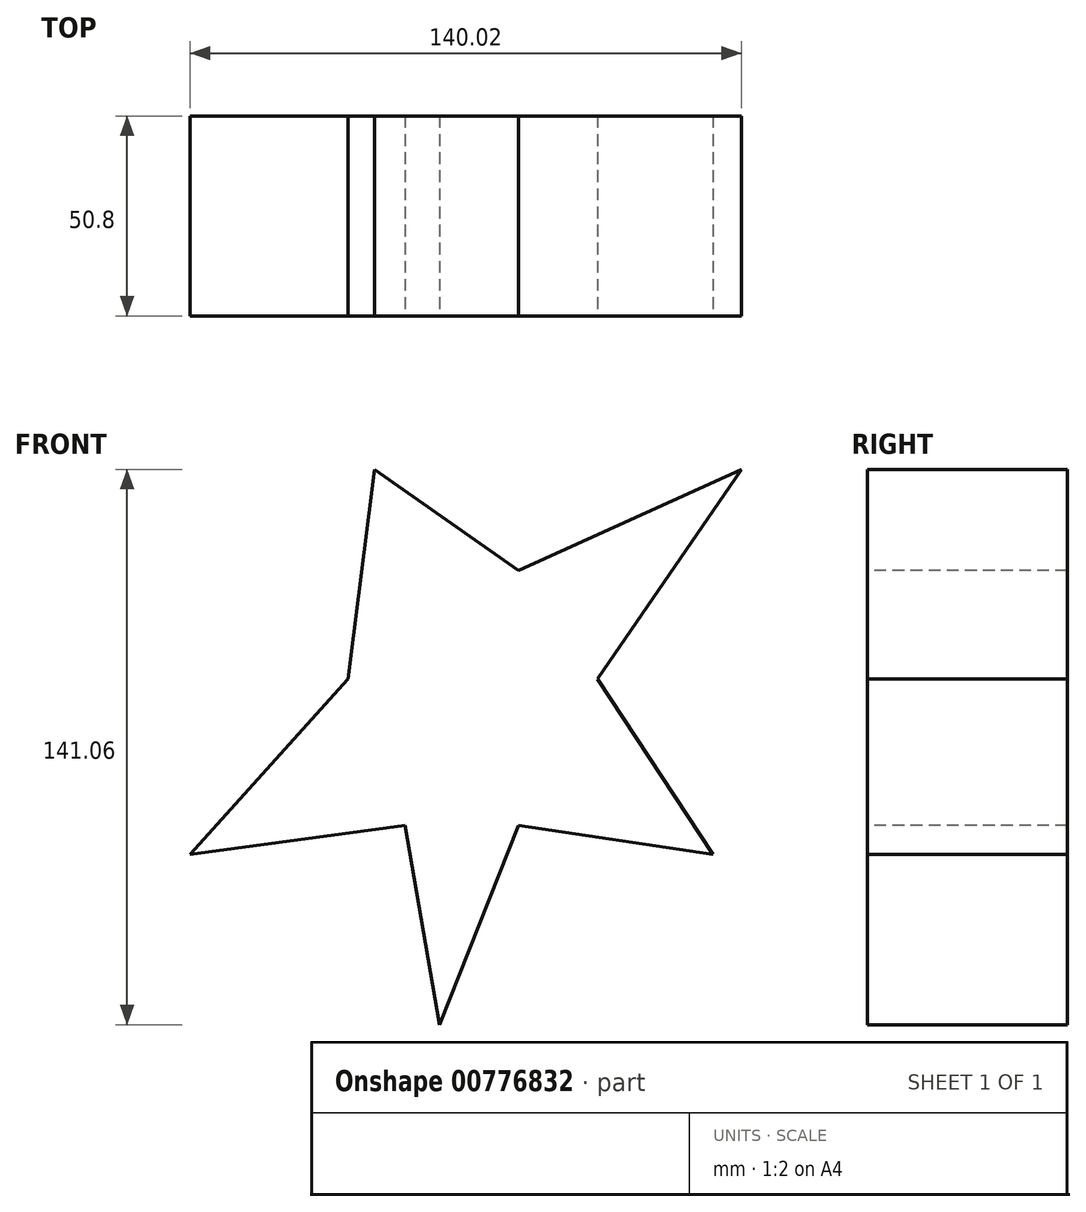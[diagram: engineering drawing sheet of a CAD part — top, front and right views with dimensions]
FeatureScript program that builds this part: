
annotation { "Feature Type Name" : "Feature", "Feature Type Description" : "" }
export const myFeature = defineFeature(function(context is Context, id is Id, definition is map)
    precondition{}
    {
        {
            var Q0;
            Q0=qCreatedBy(makeId("Front.planeOp"),FACE);
            var sketch = newSketch(context, id + "F0", { "sketchPlane" : qUnion([Q0])});
            skLineSegment(sketch, "E0", {"start": v(-6.95, -50.65) * mm, "end": v(13.13, 0) * mm});
            skLineSegment(sketch, "E1", {"start": v(13.13, 0) * mm, "end": v(62.55, -7.43) * mm});
            skLineSegment(sketch, "E2", {"start": v(62.55, -7.43) * mm, "end": v(33.2, 37.13) * mm});
            skLineSegment(sketch, "E3", {"start": v(33.2, 37.13) * mm, "end": v(69.75, 90.4) * mm});
            skLineSegment(sketch, "E4", {"start": v(69.75, 90.4) * mm, "end": v(13.13, 64.72) * mm});
            skLineSegment(sketch, "E5", {"start": v(13.13, 64.72) * mm, "end": v(-23.42, 90.4) * mm});
            skLineSegment(sketch, "E6", {"start": v(-23.42, 90.4) * mm, "end": v(-30.12, 37.13) * mm});
            skLineSegment(sketch, "E7", {"start": v(-30.12, 37.13) * mm, "end": v(-70.27, -7.43) * mm});
            skLineSegment(sketch, "E8", {"start": v(-70.27, -7.43) * mm, "end": v(-15.7, 0) * mm});
            skLineSegment(sketch, "E9", {"start": v(-6.95, -50.65) * mm, "end": v(-15.7, 0) * mm});
            skSolve(sketch);
        }
        {
            var Q0;
            Q0=makeQuery(id+"F0.imprint","IMPRINT",FACE,{"disambiguationData":[TD([[makeQuery(id+"F0.imprint","IMPRINT",EDGE,{"derivedFrom":sQuery(id+"F0.wireOp",EDGE,"E0")}),1.0]])]});
            extrude(context, id + "F1", {"entities" : qUnion([Q0]), "oppositeDirection" : true, "depth" : 50.8 * mm, "offsetDistance" : 25.4 * mm});
        }
    });
